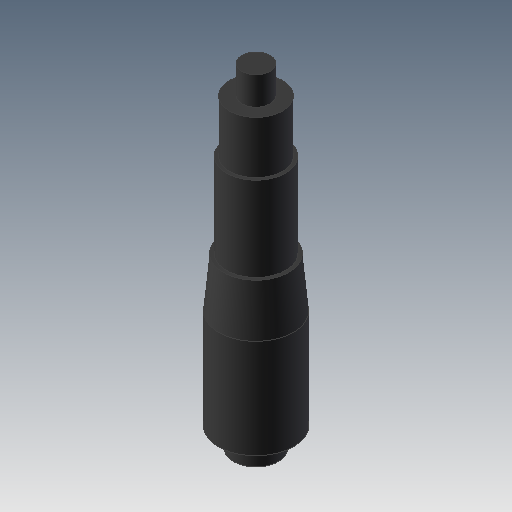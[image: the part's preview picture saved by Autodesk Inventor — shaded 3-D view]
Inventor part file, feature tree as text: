
AUTODESK INVENTOR PART (.ipt)
format: ipt  version: 2019.4 (Build 234330000, 330)  size: 117,760 bytes
history: native  units: mm
features: revolve x1, sketch x1
ambient origin geometry x8: Origin, YZ Plane, XZ Plane, XY Plane, X Axis, Y Axis, Z Axis, Center Point
bodies: Solid1 (feature_tree)
feature tree (2):
  revolve  "Revolution1"  [1 undecoded]
  sketch  "Sketch1"  dims[d0=9.3mm d1=4.725mm d2=5.0mm d3=2.5mm d4=15.0mm d5=26.5mm d6=6.65mm d7=5.27mm d8=3.6mm d9=4.0mm d10=90.0deg]
note: 1 required parameter value undecoded (feature->parameter linkage not recoverable at this tier; creation-order binding heuristic only, values carry confidence <= 0.55)
